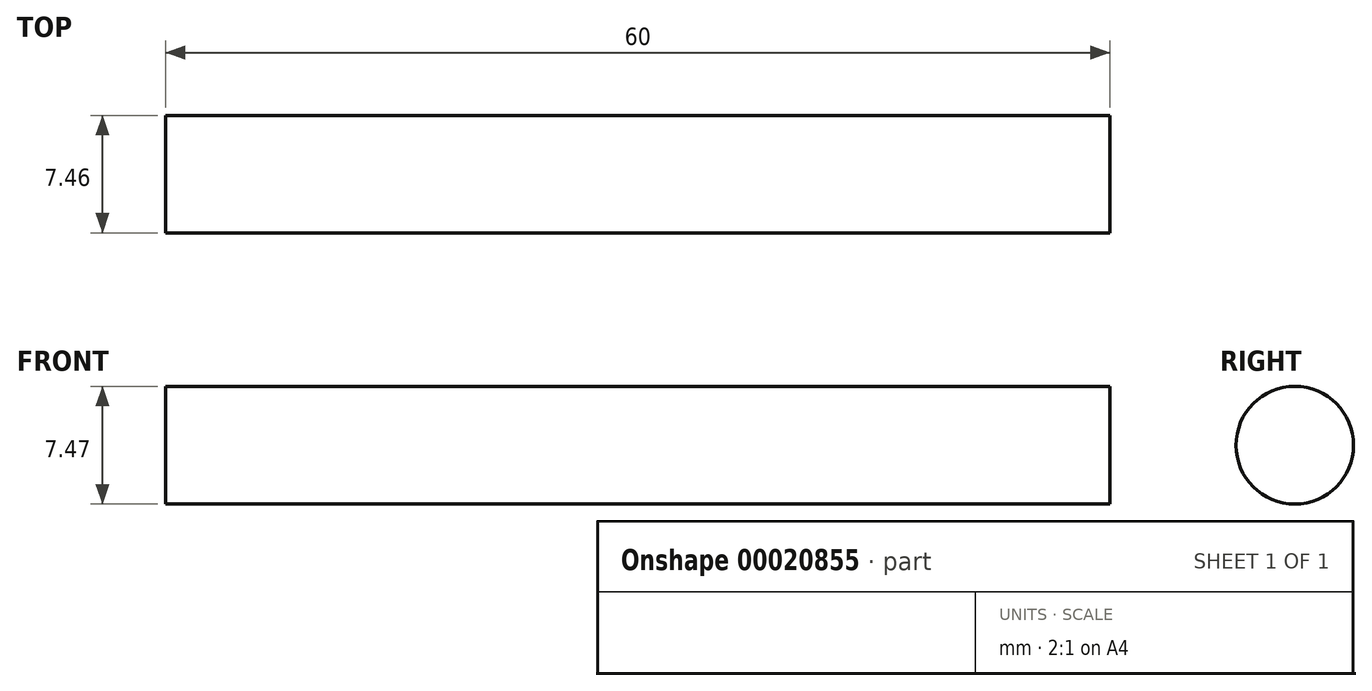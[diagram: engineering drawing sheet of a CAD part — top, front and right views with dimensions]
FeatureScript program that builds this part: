
annotation { "Feature Type Name" : "Feature", "Feature Type Description" : "" }
export const myFeature = defineFeature(function(context is Context, id is Id, definition is map)
    precondition{}
    {
        {
            var Q0;
            Q0=qCreatedBy(makeId("Right.planeOp"),FACE);
            var sketch = newSketch(context, id + "F0", { "sketchPlane" : qUnion([Q0])});
            skCircle(sketch, "E0", {"center": v(0, 4.27) * mm, "radius": 3.73 * mm});
            skSolve(sketch);
        }
        {
            var Q0;
            Q0 = qSketchRegion(id + "F0", true);
            extrude(context, id + "F1", {"entities" : qUnion([Q0]), "endBound" : BoundingType.SYMMETRIC, "depth" : 60 * mm});
        }
    });
